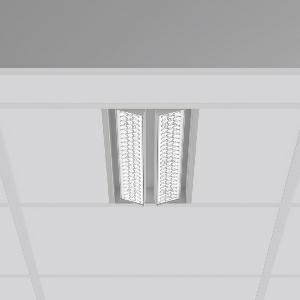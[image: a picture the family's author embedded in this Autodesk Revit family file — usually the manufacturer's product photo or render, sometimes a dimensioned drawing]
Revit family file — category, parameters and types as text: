
# Revit family: tx-move_901738_004_1_c3c0
name_source: partatom
category: Lighting Fixtures
units: mm (PartAtom-declared; Revit-internal decimal feet)

## family parameters
Cut with Voids When Loaded = No
Host = Face
Light Source = No
Part Type = Normal
Room Calculation Point = No
Round Connector Dimension = Use Diameter
Shared = No

## types (1)
- MultiLumen 1 (1 x LED Modul 840, 2675 lm, 4000)
    Apparent Load = 35 VA
    Approval mark = CE
    CIE Flux Codes = 65 90 98 100 100
    Color Rendering = 80
    Color Temperature = 4000
    Default Elevation = 1800 mm
    Description = Series: TX-MOVE
Einlege/Einbau-Flächenstrahler. Housing: sheet steel, powder-coated. 2xSwivel range: 90°. High-efficiency LED units with optimum light control thanks to clear plastic (PC) lens optics. Spezielle Mikrostrukturen reduzieren Gelbsaum. Asymmetrical light distribution. Suitable for laying in grid ceiling module 625. Connected converter included in separate gearbox.Suitable for through-wiring.MultiLumen: Luminous flux adjustable in 3 steps. Accessories: Mounting frame for installation in suspended ceilings. Environmentally friendly and resource-saving due to replaceable and recyclable components. 
Colour: silver, matt (approx. RAL 9006)
Length: 622 mm
Width: 190 mm
Height: 39 mm
Cut-out length: 602 mm
Cut-out width: 174 mm
Recess height: 100 mm
Lamp: LED
Socket: without socket
Colour temperature: 4000K
Colour rendering index (CRI): 80
System power: 35 W
Rated luminous flux: 5350 lm
Luminous efficiency: 153 lm/W
System power 2: 47 W
Rated luminous flux 2: 6950 lm
Luminous efficiency 2: 148 lm/W
System power 3: 68 W
Rated luminous flux 3: 9600 lm
Luminous efficiency 3: 141 lm/W
Control gear: Regulated power supply
Protection class: I
Type of protection: IP 20
    Height = 0 mm  [stored 0 ft]
    Lamp = 1 x LED Modul 840
    Lamp Light Flux = 2675 lm
    Lamp count = 1
    Length = 622 mm
    Lifetime = 50000 h
    Luminous efficacy = 153 lm/W
    Manufacturer = RZB
    ModVariant = No
    Model = 901738.004.1
    Mounting Place = Ceiling, Wall
    Mounting Type = Recessed
    Number of Poles = 1
    OnlyDefault = Yes
    Power Factor = 1
    Product Name = TX-MOVE
    Product group = Recessed projectors
    ProductGroupID = 401
    Protection Class = Protection class I
    Protection Degree = IP 20
    RLX_Detail_Level = 1
    RLX_Emergency_Light_Flux = 0 lm
    RLX_Emergency_Type = 0
    RLX_Emergency_Type_DB = No
    RlxData = <blob elided: 55273 chars, md5=81c9e0c3>
    Socket = socket
    Standby Power = 0 W
    System Light Flux = 5350 lm
    System Power = 35 W
    Type Comments = MultiLumen 1
    Type Image = 901737.004.jpg
    URL = http://relux.com
    VarID = multilumen_1
    Voltage = 230 V
    Voltage Range = 220-240 V
    Weight = 0.00 kg
    Width = 190 mm  [stored 0.62336 ft]

note: [stored X ft] marks values corroborated as IEEE doubles in the binary element streams (Revit-internal decimal feet)

## geometry (parser evidence)
native form markers: Blend x4, Sweep x14
no freeform markers — native parametric forms only
